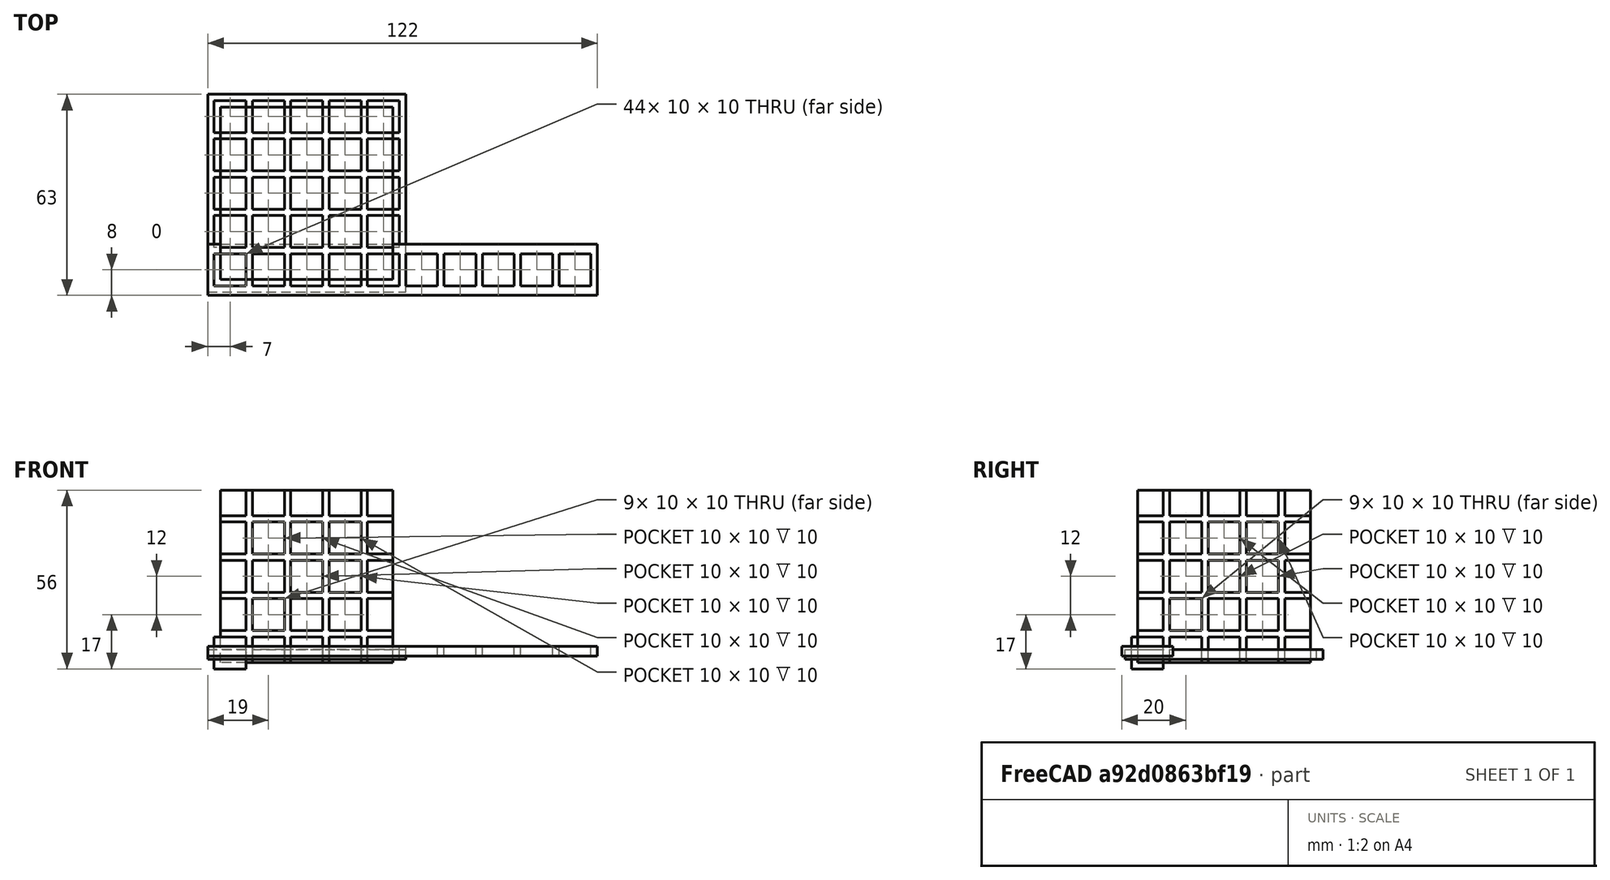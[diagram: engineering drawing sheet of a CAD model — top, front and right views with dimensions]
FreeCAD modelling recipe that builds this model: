
FCSTD DOCUMENT  (FreeCAD 1.0R39285 (Git))
Label: ojt1_t10p01_array
License: All rights reserved
objects: Part::Box×6, Part::FeaturePython×3, Part::Cut×3
note: 9 computed .brp shape members not serialized (recipe doc carries the construction recipe); baked Part::Feature solids carry a one-line shape summary decoded from their .brp

FEATURE [Part::Box] Box  label="Cub"
  AttacherType = Attacher::AttachEngine3D
  Height = 10
  Length = 10
  Width = 10
FEATURE [Part::FeaturePython] Array  # Draft array (typed FeaturePython)
  AlwaysSyncPlacement = false
  Angle = 360
  ArrayType = 0
  Axis = (0,0,1)
  Base = -> Box
  Center = (0,0,0)
  Count = 10
  ExpandArray = false
  Fuse = false
  IntervalAxis = (0,0,0)
  IntervalX = (12,0,0)
  IntervalY = (0,100,0)
  IntervalZ = (0,0,100)
  NumberCircles = 3
  NumberPolar = 5
  NumberX = 10
  NumberY = 1
  NumberZ = 1
  PlacementList = 10 placements: arithmetic series from (0,0,0) step (12,0,0) to (108,0,0)
  RadialDistance = 50
  ScaleList = (10) [(1,1,1),(1,1,1),(1,1,1),(1,1,1),(1,1,1),(1,1,1),(1,1,1),(1,1,1),(1,1,1),(1,1,1)]
  Symmetry = 1
  TangentialDistance = 25
FEATURE [Part::Box] Box001  label="Cub001"
  AttacherType = Attacher::AttachEngine3D
  Height = 3
  Length = 122
  Placement = pos=(-2,-3,4) rot=(0,0,1;0rad)
  Width = 16
FEATURE [Part::Cut] Cut  label="array_1d"
  Base = -> Box001
  Refine = true
  Tool = -> Array
FEATURE [Part::Box] Box002  label="Cub002"
  AttacherType = Attacher::AttachEngine3D
  Height = 10
  Length = 10
  Width = 10
FEATURE [Part::FeaturePython] Array001  # Draft array (typed FeaturePython)
  AlwaysSyncPlacement = false
  Angle = 360
  ArrayType = 0
  Axis = (0,0,1)
  Base = -> Box002
  Center = (0,0,0)
  Count = 25
  ExpandArray = false
  Fuse = false
  IntervalAxis = (0,0,0)
  IntervalX = (12,0,0)
  IntervalY = (0,12,0)
  IntervalZ = (0,0,100)
  NumberCircles = 3
  NumberPolar = 5
  NumberX = 5
  NumberY = 5
  NumberZ = 1
  PlacementList = 25 placements: [(0,0,0),(0,12,0),(0,24,0),(0,36,0),(0,48,0),(12,0,0),(12,12,0),(12,24,0),(12,36,0),(12,48,0),(24,0,0),(24,12,0),(24,24,0),(24,36,0),(24,48,0),(36,0,0),(36,12,0),(36,24,0),(36,36,0),(36,48,0),(48,0,0),(48,12,0),(48,24,0),(48,36,0),(48,48,0)]
  RadialDistance = 50
  ScaleList = (25) [(1,1,1),(1,1,1),(1,1,1),(1,1,1),(1,1,1),(1,1,1),(1,1,1),(1,1,1),(1,1,1),(1,1,1),(1,1,1),(1,1,1),(1,1,1),(1,1,1),(1,1,1),(1,1,1),(1,1,1),(1,1,1),+7 more]
  Symmetry = 1
  TangentialDistance = 25
FEATURE [Part::Box] Box003  label="Cub003"
  AttacherType = Attacher::AttachEngine3D
  Height = 3
  Length = 62
  Placement = pos=(-2,-2,3) rot=(0,0,1;0rad)
  Width = 62
FEATURE [Part::Cut] Cut001  label="array_2d"
  Base = -> Box003
  Refine = true
  Tool = -> Array001
FEATURE [Part::Box] Box004  label="Cub004"
  AttacherType = Attacher::AttachEngine3D
  Height = 10
  Length = 10
  Width = 10
FEATURE [Part::FeaturePython] Array002  # Draft array (typed FeaturePython)
  AlwaysSyncPlacement = false
  Angle = 360
  ArrayType = 0
  Axis = (0,0,1)
  Base = -> Box004
  Center = (0,0,0)
  Count = 125
  ExpandArray = false
  Fuse = false
  IntervalAxis = (0,0,0)
  IntervalX = (12,0,0)
  IntervalY = (0,12,0)
  IntervalZ = (0,0,12)
  NumberCircles = 3
  NumberPolar = 5
  NumberX = 5
  NumberY = 5
  NumberZ = 5
  PlacementList = 125 placements: [(0,0,0),(0,0,12),(0,0,24),(0,0,36),(0,0,48),(0,12,0),(0,12,12),(0,12,24),(0,12,36),(0,12,48),(0,24,0),(0,24,12),(0,24,24),(0,24,36),(0,24,48),(0,36,0),(0,36,12),(0,36,24),(0,36,36),(0,36,48),(0,48,0),(0,48,12),(0,48,24),(0,48,36),(0,48,48),(12,0,0),(12,0,12),(12,0,24),(12,0,36),(12,0,48),(12,12,0),(12,12,12),(12,12,24),(12,12,36),(12,12,48),(12,24,0),(12,24,12),(12,24,24),(12,24,36),(12,24,48),+85 more]
  RadialDistance = 50
  Symmetry = 1
  TangentialDistance = 25
FEATURE [Part::Box] Box005  label="Cub005"
  AttacherType = Attacher::AttachEngine3D
  Height = 54
  Length = 54
  Placement = pos=(2,2,2) rot=(0,0,1;0rad)
  Width = 54
FEATURE [Part::Cut] Cut002  label="array_3d"
  Base = -> Box005
  Refine = true
  Tool = -> Array002
